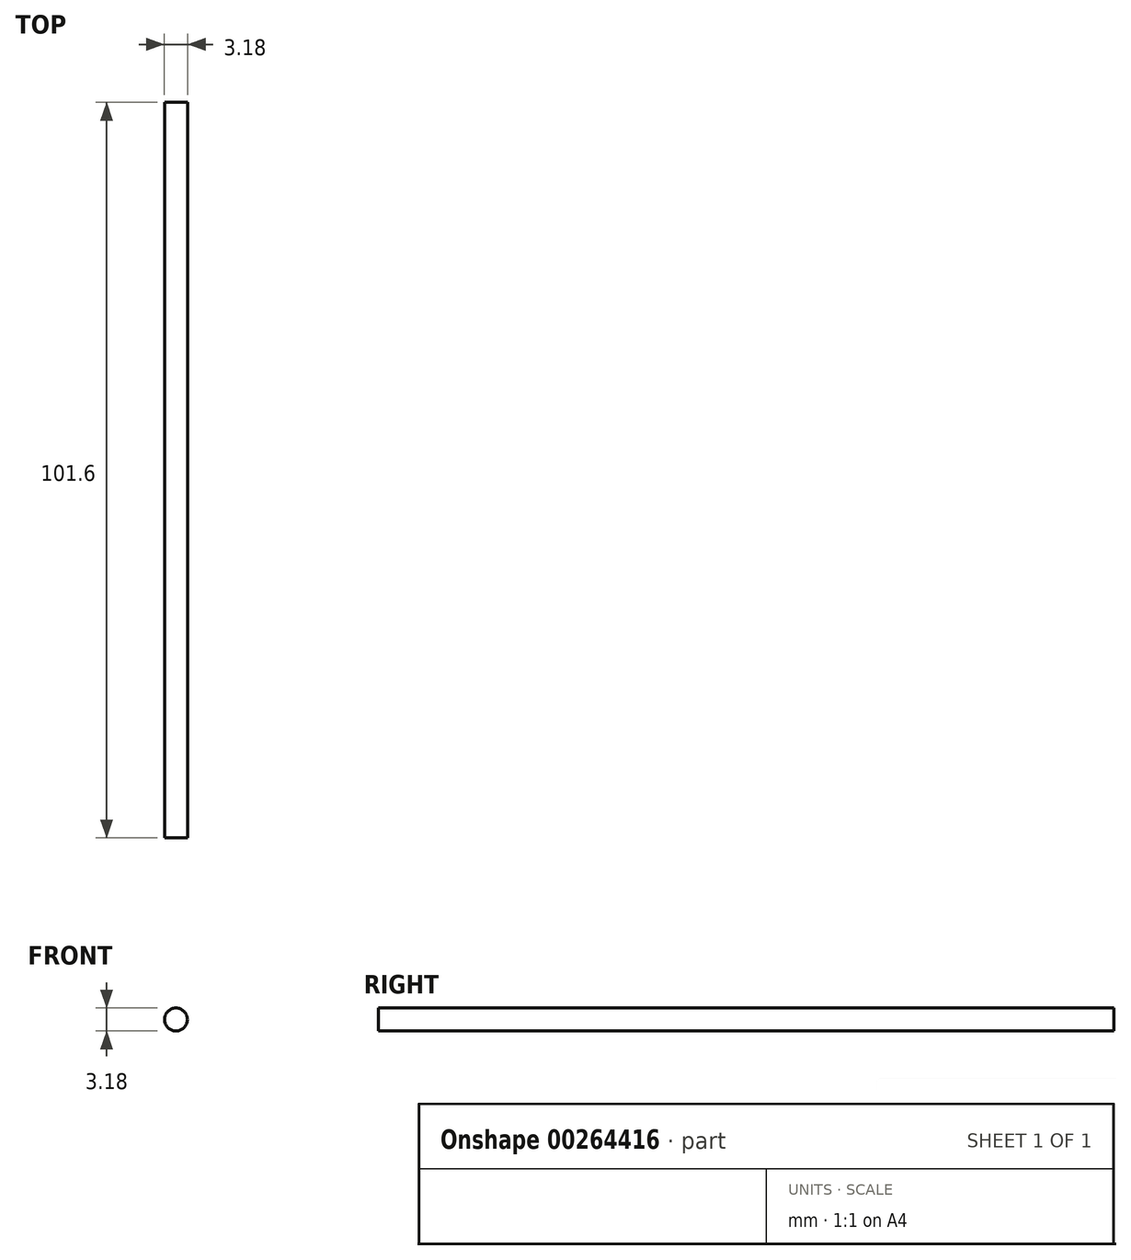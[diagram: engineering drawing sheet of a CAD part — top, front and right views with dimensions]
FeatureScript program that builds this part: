
annotation { "Feature Type Name" : "Feature", "Feature Type Description" : "" }
export const myFeature = defineFeature(function(context is Context, id is Id, definition is map)
    precondition{}
    {
        {
            var Q0;
            Q0=qCreatedBy(makeId("Front.planeOp"),FACE);
            var sketch = newSketch(context, id + "F0", { "sketchPlane" : qUnion([Q0])});
            skCircle(sketch, "E0", {"center": v(0, 0) * mm, "radius": 1.59 * mm});
            skSolve(sketch);
        }
        {
            var Q0;
            Q0=qSketchRegion(id+"F0",true);
            extrude(context, id + "F1", {"entities" : qUnion([Q0]), "depth" : 63.5 * mm});
        }
        {
            var Q0;
            Q0 = qSketchRegion(id + "F0", true);
            extrude(context, id + "F2", {"entities" : qUnion([Q0]), "operationType" : NewBodyOperationType.ADD, "oppositeDirection" : true, "depth" : 38.1 * mm});
        }
    });
